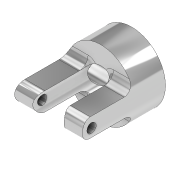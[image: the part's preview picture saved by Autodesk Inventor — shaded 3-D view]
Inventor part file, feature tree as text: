
AUTODESK INVENTOR PART (.ipt)
format: ipt  version: 2020 (Build 240168000, 168)  size: 184,832 bytes
history: native  units: in
note: dims shown in document units (in); Inventor stores cm internally (conversion verified against a paired STEP export)
features: extrude x4, sketch x4, fillet x1, projected_geometry x1
ambient origin geometry x8: Origin, YZ Plane, XZ Plane, XY Plane, X Axis, Y Axis, Z Axis, Center Point
bodies: Solid1 (feature_tree)
feature tree (10):
  extrude  "Extrusion1"  Depth=0.4331in
  extrude  "Extrusion2"  Depth=0.0591in
  fillet  "Fillet1"  Radius=0.1181in
  extrude  "Extrusion3"  Depth=0.3346in TaperAngle=0.0deg
  extrude  "Extrusion4"  Depth=0.0591in
  sketch  "Sketch1"  dims[d0=0.2008in d1=0.4331in]
  sketch  "Sketch2"  dims[d2=0.1969in d3=0.0in d4=0.0591in d5=0.1181in]
  projected_geometry  "Projected Loop1"
  sketch  "Sketch3"  dims[d6=0.0in d7=0.3346in d8=0.0in]
  sketch  "Sketch4"  dims[d9=0.0591in d10=0.0591in d11=0.1654in d12=0.374in d13=0.0in d14=0.374in d15=0.0in]
